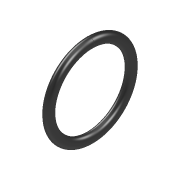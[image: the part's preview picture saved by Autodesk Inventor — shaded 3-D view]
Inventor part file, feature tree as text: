
AUTODESK INVENTOR PART (.ipt)
format: ipt  version: 2022.3 (Build 263350000, 350)  size: 141,824 bytes
history: native  units: mm
features: sketch x2, other x1, sweep x1
ambient origin geometry x8: Origin, YZ Plane, XZ Plane, XY Plane, X Axis, Y Axis, Z Axis, Center Point
bodies: Body1 (feature_tree)
feature tree (4):
  other  "Sólido1"
  sweep  "Barrido1"
  sketch  "Boceto1"  dims[d0=1.0mm d1=1.2mm]
  sketch  "Boceto2"  dims[d2=9.9mm d3=0.0mm d4=0.0mm]
